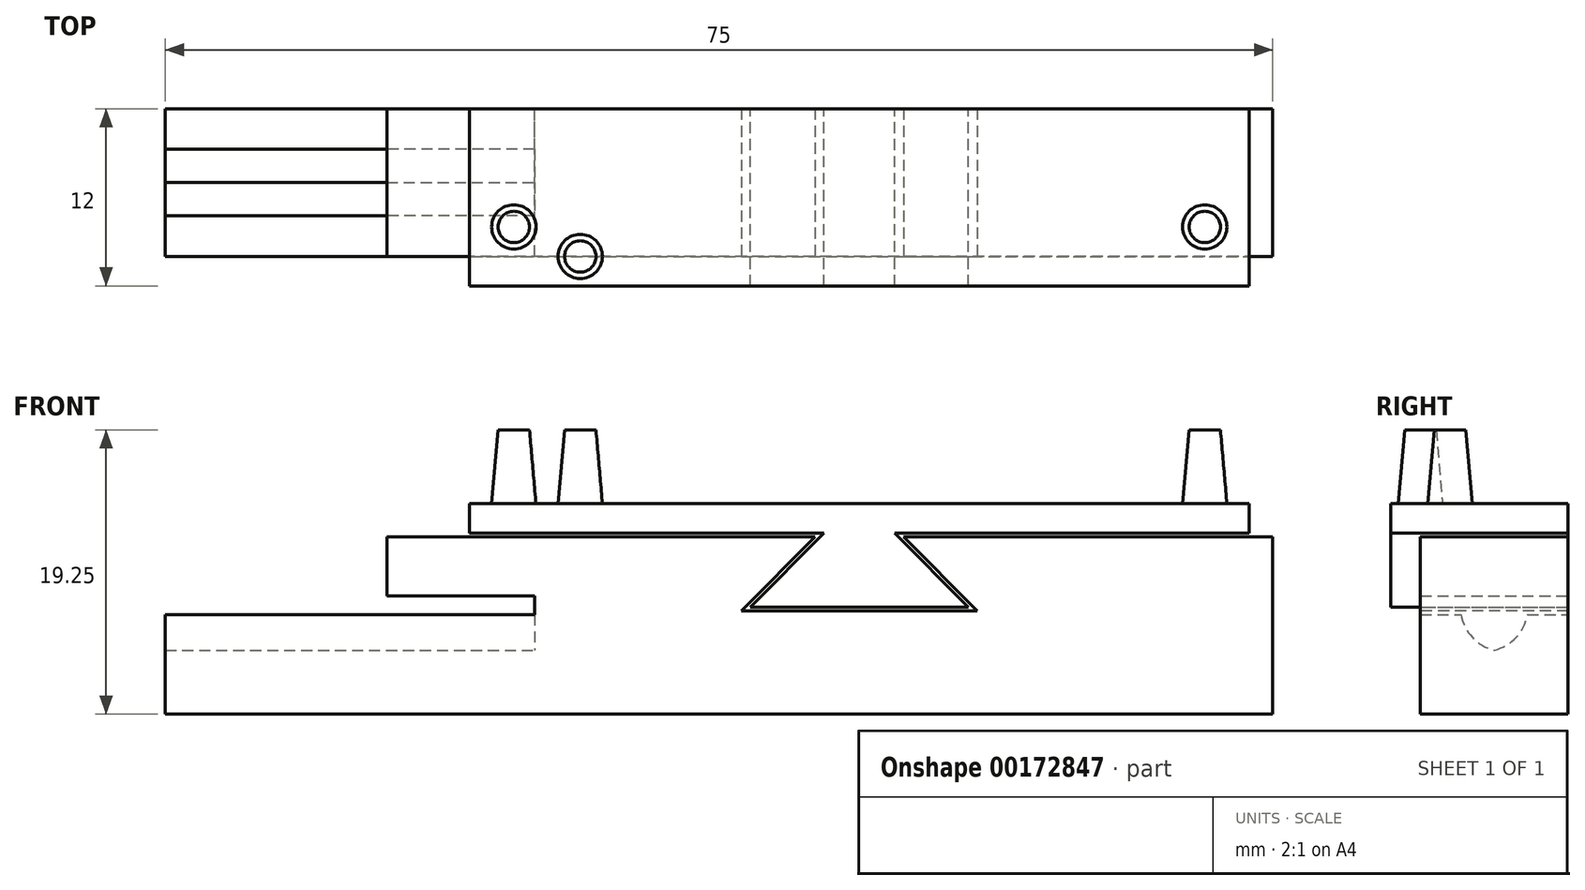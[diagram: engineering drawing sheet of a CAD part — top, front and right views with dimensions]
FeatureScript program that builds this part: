
annotation { "Feature Type Name" : "Feature", "Feature Type Description" : "" }
export const myFeature = defineFeature(function(context is Context, id is Id, definition is map)
    precondition{}
    {
        {
            var Q0;
            Q0=qCreatedBy(makeId("Front.planeOp"),FACE);
            var sketch = newSketch(context, id + "F0", { "sketchPlane" : qUnion([Q0])});
            skLineSegment(sketch, "E0", {"start": v(0, 0) * mm, "end": v(0, -12) * mm});
            skLineSegment(sketch, "E1", {"start": v(0, -12) * mm, "end": v(-5, -12) * mm});
            skLineSegment(sketch, "E2", {"start": v(-5, -12) * mm, "end": v(-5, -9.28) * mm, "construction": true});
            skLineSegment(sketch, "E3", {"start": v(-5, -9.28) * mm, "end": v(-70, -9.28) * mm, "construction": true});
            skLineSegment(sketch, "E4", {"start": v(-70, -9.28) * mm, "end": v(-70, -12) * mm, "construction": true});
            skLineSegment(sketch, "E5", {"start": v(-70, -12) * mm, "end": v(-75, -12) * mm});
            skLineSegment(sketch, "E6", {"start": v(-75, -12) * mm, "end": v(-75, -5.25) * mm});
            skLineSegment(sketch, "E7", {"start": v(-75, -5.25) * mm, "end": v(-50, -5.25) * mm});
            skLineSegment(sketch, "E8", {"start": v(-50, -5.25) * mm, "end": v(-50, -4) * mm});
            skLineSegment(sketch, "E9", {"start": v(-50, -4) * mm, "end": v(-60, -4) * mm});
            skLineSegment(sketch, "E10", {"start": v(-60, -4) * mm, "end": v(-60, 0) * mm});
            skLineSegment(sketch, "E11", {"start": v(-60, 0) * mm, "end": v(0, 0) * mm});
            skLineSegment(sketch, "E12", {"start": v(-70, -12) * mm, "end": v(-5, -12) * mm});
            skSolve(sketch);
        }
        {
            var Q0;
            Q0 = qSketchRegion(id + "F0", true);
            extrude(context, id + "F1", {"entities" : qUnion([Q0]), "depth" : 10 * mm});
        }
        {
            var Q0;
            Q0=makeQuery(id+"F1.opExtrude","SWEPT_FACE",FACE,{"disambiguationData":[OSD([sQuery(id+"F0.wireOp",EDGE,"E7")])]});
            var sketch = newSketch(context, id + "F2", { "sketchPlane" : qUnion([Q0])});
            skLineSegment(sketch, "E13.bottom", {"start": v(-50, -2.75) * mm, "end": v(-75, -2.75) * mm});
            skLineSegment(sketch, "E13.top", {"start": v(-50, -7.25) * mm, "end": v(-75, -7.25) * mm});
            skLineSegment(sketch, "E13.left", {"start": v(-50, -2.75) * mm, "end": v(-50, -7.25) * mm});
            skPoint(sketch, "E13.middle", {"position": v(-75, -5) * mm});
            skLineSegment(sketch, "E14", {"start": v(-75, -7.25) * mm, "end": v(-75, -2.75) * mm});
            skPoint(sketch, "E13.right.start.orphan", {"position": v(-100, -2.75) * mm});
            skPoint(sketch, "E15.orphan", {"position": v(-100, -7.25) * mm});
            skSolve(sketch);
        }
        {
            var Q0;
            Q0 = qSketchRegion(id + "F2", true);
            extrude(context, id + "F3", {"entities" : qUnion([Q0]), "operationType" : NewBodyOperationType.REMOVE, "oppositeDirection" : true, "depth" : 2.5 * mm});
        }
        {
            var Q0;
            {var subQ2=sQuery(id+"F0.wireOp",EDGE,"E7");Q0=makeQuery(id+"F3.boolean.opBoolean","SPLIT",FACE,{"disambiguationData":[TD([makeQuery(id+"F3.opExtrude","SWEPT_FACE",FACE,{"disambiguationData":[OSD([sQuery(id+"F2.wireOp",EDGE,"E13.bottom")])]})])],"derivedFrom":makeQuery(id+"F1.opExtrude","SWEPT_FACE",FACE,{"disambiguationData":[OSD([subQ2])]})});}
            cPlane(context, id + "F4", {"entities" : qUnion([Q0]), "cplaneType" : CPlaneType.OFFSET, "offset" : 0 * mm, "width" : 150 * mm, "height" : 150 * mm});
        }
        {
            var Q0;
            Q0=makeQuery(id+"F1.opExtrude","CAP_FACE",FACE,{"disambiguationData":[OSD([sQuery(id+"F0.wireOp",EDGE,"E0"),sQuery(id+"F0.wireOp",EDGE,"E1"),sQuery(id+"F0.wireOp",EDGE,"E5"),sQuery(id+"F0.wireOp",EDGE,"E6"),sQuery(id+"F0.wireOp",EDGE,"E7"),sQuery(id+"F0.wireOp",EDGE,"E8"),sQuery(id+"F0.wireOp",EDGE,"E9"),sQuery(id+"F0.wireOp",EDGE,"E10"),sQuery(id+"F0.wireOp",EDGE,"E11"),sQuery(id+"F0.wireOp",EDGE,"E12")])],"isStart":false});
            var sketch = newSketch(context, id + "F5", { "sketchPlane" : qUnion([Q0])});
            skLineSegment(sketch, "E16", {"start": v(-28, 0) * mm, "end": v(-28, -8.66) * mm, "construction": true});
            skLineSegment(sketch, "E17", {"start": v(-31, 0) * mm, "end": v(-36, -5) * mm});
            skLineSegment(sketch, "E18", {"start": v(-36, -5) * mm, "end": v(-28, -5) * mm});
            skLineSegment(sketch, "E19", {"start": v(-31, 0) * mm, "end": v(-28, 0) * mm});
            skLineSegment(sketch, "E20.MirrorCS", {"start": v(-25, 0) * mm, "end": v(-28, 0) * mm});
            skLineSegment(sketch, "E21.MirrorCS", {"start": v(-25, 0) * mm, "end": v(-20, -5) * mm});
            skLineSegment(sketch, "E22.MirrorCS", {"start": v(-20, -5) * mm, "end": v(-28, -5) * mm});
            skSolve(sketch);
        }
        {
            var Q0;
            Q0 = qSketchRegion(id + "F5", true);
            extrude(context, id + "F6", {"entities" : qUnion([Q0]), "operationType" : NewBodyOperationType.REMOVE, "endBound" : BoundingType.THROUGH_ALL, "oppositeDirection" : true, "depth" : 25 * mm});
        }
        {
            var Q0;
            Q0=makeQuery(id+"F3.boolean.opBoolean","COPY",EDGE,{"derivedFrom":makeQuery(id+"F3.opExtrude","CAP_EDGE",EDGE,{"disambiguationData":[OSD([sQuery(id+"F2.wireOp",EDGE,"E13.bottom")])],"isStart":false})});
            var Q1;
            Q1=makeQuery(id+"F3.boolean.opBoolean","COPY",EDGE,{"derivedFrom":makeQuery(id+"F3.opExtrude","CAP_EDGE",EDGE,{"disambiguationData":[OSD([sQuery(id+"F2.wireOp",EDGE,"E13.top")])],"isStart":false})});
            fillet(context, id + "F7", {"entities" : qUnion([Q0, Q1]), "radius" : 3 * mm, "tangentPropagation" : true, "allowEdgeOverflow" : false});
        }
        {
            var Q0;
            Q0=qCreatedBy(makeId("Front.planeOp"),FACE);
            var sketch = newSketch(context, id + "F8", { "sketchPlane" : qUnion([Q0])});
            skLineSegment(sketch, "E23.0", {"start": v(-25.6, 0.25) * mm, "end": v(-20.6, -4.75) * mm});
            skLineSegment(sketch, "E24.0", {"start": v(-30.4, 0.25) * mm, "end": v(-35.4, -4.75) * mm});
            skLineSegment(sketch, "E25.0", {"start": v(-35.4, -4.75) * mm, "end": v(-20.6, -4.75) * mm});
            skLineSegment(sketch, "E26.0", {"start": v(-25.6, 0.25) * mm, "end": v(-1.6, 0.25) * mm});
            skLineSegment(sketch, "E27.0", {"start": v(-54.4, 0.25) * mm, "end": v(-30.4, 0.25) * mm});
            skLineSegment(sketch, "E28", {"start": v(-1.6, 0.25) * mm, "end": v(-1.6, 2.25) * mm});
            skLineSegment(sketch, "E29", {"start": v(-1.6, 2.25) * mm, "end": v(-54.4, 2.25) * mm});
            skLineSegment(sketch, "E30", {"start": v(-54.4, 2.25) * mm, "end": v(-54.4, 0.25) * mm});
            skSolve(sketch);
        }
        {
            var Q0;
            Q0 = qSketchRegion(id + "F8", true);
            var Q1;
            Q1=makeQuery(id+"F1.opExtrude","CAP_FACE",FACE,{"disambiguationData":[OSD([sQuery(id+"F0.wireOp",EDGE,"E0"),sQuery(id+"F0.wireOp",EDGE,"E1"),sQuery(id+"F0.wireOp",EDGE,"E5"),sQuery(id+"F0.wireOp",EDGE,"E6"),sQuery(id+"F0.wireOp",EDGE,"E7"),sQuery(id+"F0.wireOp",EDGE,"E8"),sQuery(id+"F0.wireOp",EDGE,"E9"),sQuery(id+"F0.wireOp",EDGE,"E10"),sQuery(id+"F0.wireOp",EDGE,"E11"),sQuery(id+"F0.wireOp",EDGE,"E12")])],"isStart":false});
            extrude(context, id + "F9", {"entities" : qUnion([Q0]), "endBoundEntityFace" : qUnion([Q1]), "depth" : 12 * mm});
        }
        {
            var Q0;
            Q0=makeQuery(id+"F9.opExtrude","SWEPT_FACE",FACE,{"disambiguationData":[OSD([sQuery(id+"F8.wireOp",EDGE,"E29")])]});
            var sketch = newSketch(context, id + "F10", { "sketchPlane" : qUnion([Q0])});
            skCircle(sketch, "E31", {"center": v(-46.9, -10) * mm, "radius": 1.5 * mm});
            skCircle(sketch, "E32", {"center": v(-51.4, -8) * mm, "radius": 1.5 * mm});
            skCircle(sketch, "E33", {"center": v(-4.6, -8) * mm, "radius": 1.5 * mm});
            skSolve(sketch);
        }
        {
            var Q0;
            Q0 = qSketchRegion(id + "F10", true);
            extrude(context, id + "F11", {"entities" : qUnion([Q0]), "depth" : 5 * mm, "hasDraft" : true, "draftAngle" : 5 * degree, "draftPullDirection" : true});
        }
    });
